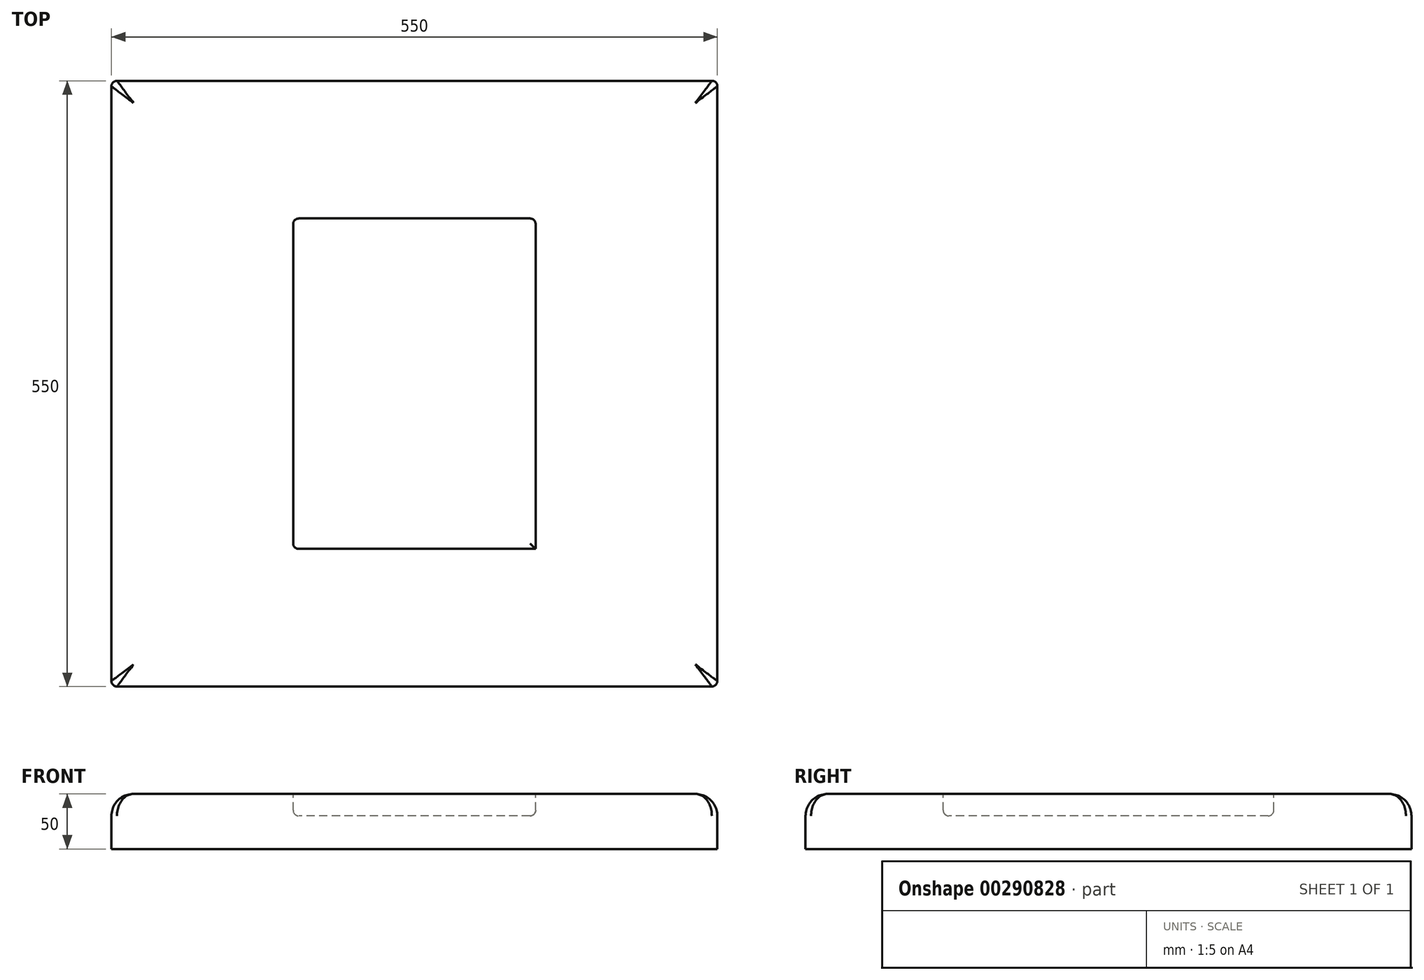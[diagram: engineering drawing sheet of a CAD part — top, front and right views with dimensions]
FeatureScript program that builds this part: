
annotation { "Feature Type Name" : "Feature", "Feature Type Description" : "" }
export const myFeature = defineFeature(function(context is Context, id is Id, definition is map)
    precondition{}
    {
        {
            var Q0;
            Q0=qCreatedBy(makeId("Top.planeOp"),FACE);
            var sketch = newSketch(context, id + "F0", { "sketchPlane" : qUnion([Q0])});
            skLineSegment(sketch, "E0.bottom", {"start": v(-275, 275) * mm, "end": v(275, 275) * mm});
            skLineSegment(sketch, "E0.top", {"start": v(-275, -275) * mm, "end": v(275, -275) * mm});
            skLineSegment(sketch, "E0.left", {"start": v(-275, 275) * mm, "end": v(-275, -275) * mm});
            skLineSegment(sketch, "E0.right", {"start": v(275, 275) * mm, "end": v(275, -275) * mm});
            skPoint(sketch, "E0.middle", {"position": v(0, 0) * mm});
            skSolve(sketch);
        }
        {
            var Q0;
            Q0=makeQuery(id+"F0.imprint","IMPRINT",FACE,{"disambiguationData":[TD([[makeQuery(id+"F0.imprint","IMPRINT",EDGE,{"derivedFrom":sQuery(id+"F0.wireOp",EDGE,"E0.bottom")}),-1.0]])]});
            extrude(context, id + "F1", {"entities" : qUnion([Q0]), "depth" : 50 * mm});
        }
        {
            var Q0;
            Q0=makeQuery(id+"F1.opExtrude","CAP_EDGE",EDGE,{"disambiguationData":[OSD([sQuery(id+"F0.wireOp",EDGE,"E0.left")])],"isStart":false});
            var Q1;
            Q1=makeQuery(id+"F1.opExtrude","CAP_EDGE",EDGE,{"disambiguationData":[OSD([sQuery(id+"F0.wireOp",EDGE,"E0.right")])],"isStart":false});
            var Q2;
            Q2=makeQuery(id+"F1.opExtrude","CAP_EDGE",EDGE,{"disambiguationData":[OSD([sQuery(id+"F0.wireOp",EDGE,"E0.bottom")])],"isStart":false});
            var Q3;
            Q3=makeQuery(id+"F1.opExtrude","CAP_EDGE",EDGE,{"disambiguationData":[OSD([sQuery(id+"F0.wireOp",EDGE,"E0.top")])],"isStart":false});
            fillet(context, id + "F2", {"entities" : qUnion([Q0, Q1, Q2, Q3]), "radius" : 20 * mm, "tangentPropagation" : true, "allowEdgeOverflow" : false});
        }
        {
            var Q0;
            Q0=makeQuery(id+"F1.opExtrude","CAP_FACE",FACE,{"disambiguationData":[OSD([sQuery(id+"F0.wireOp",EDGE,"E0.bottom"),sQuery(id+"F0.wireOp",EDGE,"E0.top"),sQuery(id+"F0.wireOp",EDGE,"E0.left"),sQuery(id+"F0.wireOp",EDGE,"E0.right")])],"isStart":false});
            var sketch = newSketch(context, id + "F3", { "sketchPlane" : qUnion([Q0])});
            skLineSegment(sketch, "E1.bottom", {"start": v(110, 150) * mm, "end": v(-110, 150) * mm});
            skLineSegment(sketch, "E1.top", {"start": v(110, -150) * mm, "end": v(-110, -150) * mm});
            skLineSegment(sketch, "E1.left", {"start": v(110, 150) * mm, "end": v(110, -150) * mm});
            skLineSegment(sketch, "E1.right", {"start": v(-110, 150) * mm, "end": v(-110, -150) * mm});
            skPoint(sketch, "E1.middle", {"position": v(0, 0) * mm});
            skSolve(sketch);
        }
        {
            var Q0;
            Q0=makeQuery(id+"F3.imprint","IMPRINT",FACE,{"disambiguationData":[TD([[makeQuery(id+"F3.imprint","IMPRINT",EDGE,{"derivedFrom":sQuery(id+"F3.wireOp",EDGE,"E1.bottom")}),1.0]])]});
            extrude(context, id + "F4", {"entities" : qUnion([Q0]), "operationType" : NewBodyOperationType.REMOVE, "oppositeDirection" : true, "depth" : 20 * mm});
        }
        {
            var Q0;
            Q0=makeQuery(id+"F4.boolean.opBoolean","COPY",EDGE,{"derivedFrom":makeQuery(id+"F4.opExtrude","SWEPT_EDGE",EDGE,{"disambiguationData":[OSD([sQuery(id+"F3.wireOp",EDGE,"E1.bottom"),sQuery(id+"F3.wireOp",EDGE,"E1.right")])]})});
            var Q1;
            Q1=makeQuery(id+"F4.boolean.opBoolean","COPY",EDGE,{"derivedFrom":makeQuery(id+"F4.opExtrude","SWEPT_EDGE",EDGE,{"disambiguationData":[OSD([sQuery(id+"F3.wireOp",EDGE,"E1.bottom"),sQuery(id+"F3.wireOp",EDGE,"E1.left")])]})});
            var Q2;
            Q2=makeQuery(id+"F4.boolean.opBoolean","COPY",EDGE,{"derivedFrom":makeQuery(id+"F4.opExtrude","CAP_EDGE",EDGE,{"disambiguationData":[OSD([sQuery(id+"F3.wireOp",EDGE,"E1.bottom")])],"isStart":false})});
            var Q3;
            Q3=makeQuery(id+"F4.boolean.opBoolean","COPY",EDGE,{"derivedFrom":makeQuery(id+"F4.opExtrude","CAP_EDGE",EDGE,{"disambiguationData":[OSD([sQuery(id+"F3.wireOp",EDGE,"E1.left")])],"isStart":false})});
            var Q4;
            Q4=makeQuery(id+"F4.boolean.opBoolean","COPY",EDGE,{"derivedFrom":makeQuery(id+"F4.opExtrude","CAP_EDGE",EDGE,{"disambiguationData":[OSD([sQuery(id+"F3.wireOp",EDGE,"E1.left")])],"isStart":true})});
            var Q5;
            Q5=makeQuery(id+"F4.boolean.opBoolean","COPY",EDGE,{"derivedFrom":makeQuery(id+"F4.opExtrude","CAP_EDGE",EDGE,{"disambiguationData":[OSD([sQuery(id+"F3.wireOp",EDGE,"E1.bottom")])],"isStart":true})});
            var Q6;
            Q6=makeQuery(id+"F4.boolean.opBoolean","COPY",EDGE,{"derivedFrom":makeQuery(id+"F4.opExtrude","CAP_EDGE",EDGE,{"disambiguationData":[OSD([sQuery(id+"F3.wireOp",EDGE,"E1.right")])],"isStart":false})});
            var Q7;
            Q7=makeQuery(id+"F4.boolean.opBoolean","COPY",EDGE,{"derivedFrom":makeQuery(id+"F4.opExtrude","SWEPT_EDGE",EDGE,{"disambiguationData":[OSD([sQuery(id+"F3.wireOp",EDGE,"E1.top"),sQuery(id+"F3.wireOp",EDGE,"E1.right")])]})});
            var Q8;
            Q8=makeQuery(id+"F4.boolean.opBoolean","COPY",EDGE,{"derivedFrom":makeQuery(id+"F4.opExtrude","CAP_EDGE",EDGE,{"disambiguationData":[OSD([sQuery(id+"F3.wireOp",EDGE,"E1.top")])],"isStart":false})});
            fillet(context, id + "F5", {"entities" : qUnion([Q0, Q1, Q2, Q3, Q4, Q5, Q6, Q7, Q8]), "radius" : 5 * mm, "tangentPropagation" : true, "allowEdgeOverflow" : false});
        }
        {
            var Q0;
            Q0=makeQuery(id+"F1.opExtrude","SWEPT_EDGE",EDGE,{"disambiguationData":[OSD([sQuery(id+"F0.wireOp",EDGE,"E0.top"),sQuery(id+"F0.wireOp",EDGE,"E0.right")])]});
            var Q1;
            Q1=makeQuery(id+"F1.opExtrude","SWEPT_EDGE",EDGE,{"disambiguationData":[OSD([sQuery(id+"F0.wireOp",EDGE,"E0.top"),sQuery(id+"F0.wireOp",EDGE,"E0.left")])]});
            var Q2;
            Q2=makeQuery(id+"F1.opExtrude","SWEPT_EDGE",EDGE,{"disambiguationData":[OSD([sQuery(id+"F0.wireOp",EDGE,"E0.bottom"),sQuery(id+"F0.wireOp",EDGE,"E0.right")])]});
            var Q3;
            Q3=makeQuery(id+"F1.opExtrude","SWEPT_EDGE",EDGE,{"disambiguationData":[OSD([sQuery(id+"F0.wireOp",EDGE,"E0.bottom"),sQuery(id+"F0.wireOp",EDGE,"E0.left")])]});
            fillet(context, id + "F6", {"entities" : qUnion([Q0, Q1, Q2, Q3]), "radius" : 5 * mm, "tangentPropagation" : true, "allowEdgeOverflow" : false});
        }
    });
